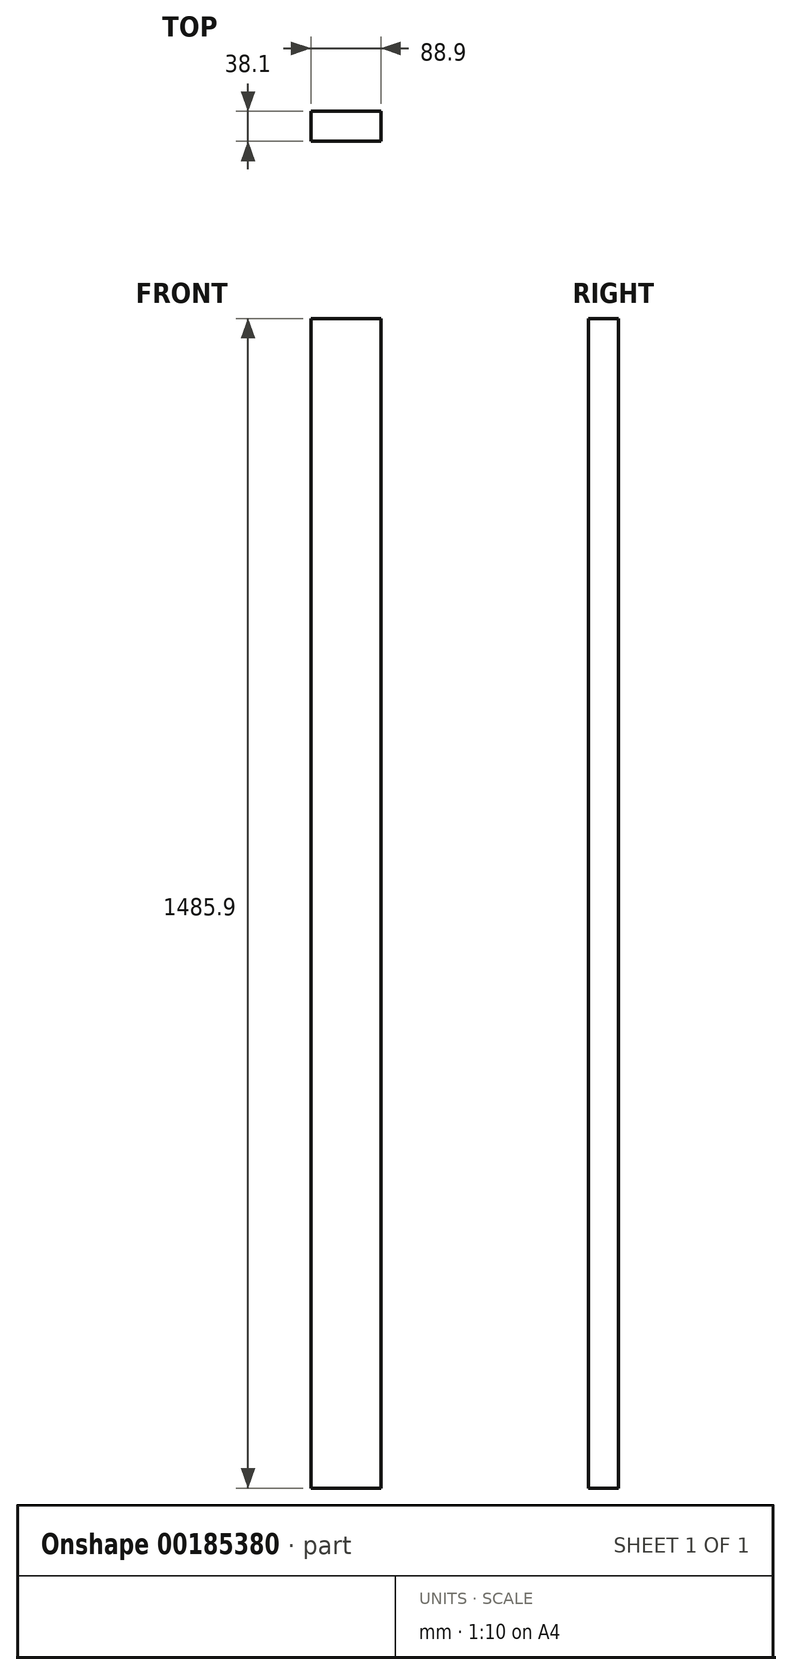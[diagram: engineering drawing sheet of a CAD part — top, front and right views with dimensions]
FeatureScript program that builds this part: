
annotation { "Feature Type Name" : "Feature", "Feature Type Description" : "" }
export const myFeature = defineFeature(function(context is Context, id is Id, definition is map)
    precondition{}
    {
        {
            var Q0;
            Q0=qCreatedBy(makeId("Top.planeOp"),FACE);
            var sketch = newSketch(context, id + "F0", { "sketchPlane" : qUnion([Q0])});
            skLineSegment(sketch, "E0.bottom", {"start": v(0, 0) * mm, "end": v(88.9, 0) * mm});
            skLineSegment(sketch, "E0.top", {"start": v(0, 38.1) * mm, "end": v(88.9, 38.1) * mm});
            skLineSegment(sketch, "E0.left", {"start": v(0, 0) * mm, "end": v(0, 38.1) * mm});
            skLineSegment(sketch, "E0.right", {"start": v(88.9, 0) * mm, "end": v(88.9, 38.1) * mm});
            skSolve(sketch);
        }
        {
            var Q0;
            Q0=makeQuery(id+"F0.imprint","IMPRINT",FACE,{"disambiguationData":[TD([[makeQuery(id+"F0.imprint","IMPRINT",EDGE,{"derivedFrom":sQuery(id+"F0.wireOp",EDGE,"E0.bottom")}),1.0]])]});
            extrude(context, id + "F1", {"entities" : qUnion([Q0]), "depth" : 1485.9 * mm});
        }
    });
